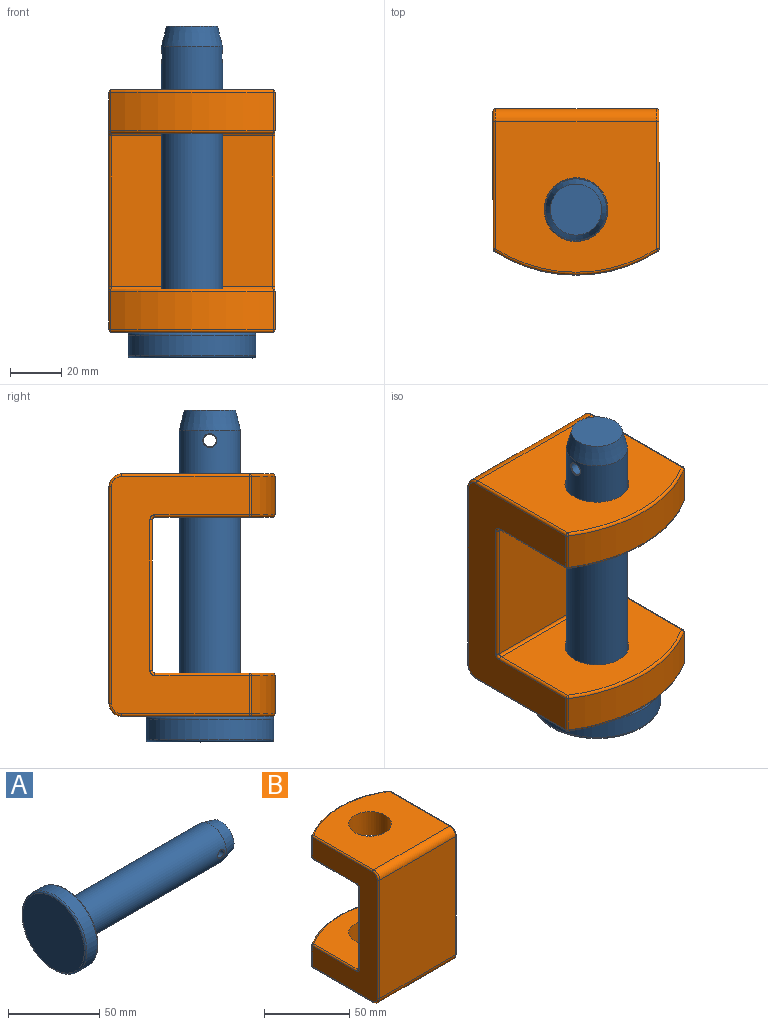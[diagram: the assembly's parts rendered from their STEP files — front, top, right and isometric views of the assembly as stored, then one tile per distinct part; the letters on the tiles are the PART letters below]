
ASSEMBLY  parts=2 mates=1
PART A: 12 faces, bbox 130x54.1x54.1 mm
  f0: cylinder r=12mm len=111mm, axis (1,0,0), area 8322.5mm2, adj f1,f8,f10,f11
  f1: torus R=13mm, axis (1,0,0), area 122mm2, adj f0,f2
  f2: plane 48x48mm, normal (1,0,0), area 1278.6mm2, adj f1,f3
  f3: torus R=24mm, axis (1,0,0), area 243.2mm2, adj f2,f4
  f4: cylinder r=25mm len=50mm, axis (1,0,0), area 1256.6mm2, adj f3,f5
  f5: torus R=24mm, axis (1,0,0), area 243.2mm2, adj f4,f6
  f6: plane 48x48mm, normal (-1,0,0), area 1809.6mm2, adj f5
  f7: plane 20x20mm, normal (1,0,0), area 314.2mm2, adj f8
  f8: cone r=10mm half-angle=14deg, axis (-1,0,0), area 569.9mm2, adj f0,f7
  f9: cylinder r=2.5mm len=23.6mm, axis (0,-1,0), area 365.8mm2, adj f10,f11
  f10: bspline ~5.5x5.4mm, area 5.5mm2, adj f0,f9
  f11: bspline ~5.5x5.4mm, area 5.5mm2, adj f0,f9
PART B: 53 faces, bbox 69.3x70.4x95.8 mm
  f0: plane 63x59mm, normal (0,0,1), area 3041.1mm2, adj f6,f12,f32,f42,f47
  f1: plane 63x59mm, normal (0,0,-1), area 2959.4mm2, adj f8,f33,f43,f48,f52
  f2: plane 63x46mm, normal (0,0,1), area 2222.1mm2, adj f9,f13,f21,f35,f36
  f3: plane 63x46mm, normal (0,0,-1), area 2222.1mm2, adj f11,f12,f19,f29,f30
  f4: plane 93x53.89mm, normal (1,0,0), area 2556.5mm2, adj f16,f17,f18,f19,f20,f21,f25,f26
  f5: plane 93x53.89mm, normal (-1,0,0), area 2556.5mm2, adj f22,f23,f28,f29,f36,f41,f44,f47
  f6: cylinder r=5mm len=63mm, axis (-1,0,0), area 494.8mm2, adj f0,f7,f25,f49
  f7: plane 85x63mm, normal (0,-1,0), area 5355mm2, adj f6,f8,f20,f51
  f8: cylinder r=5mm len=63mm, axis (-1,0,0), area 494.8mm2, adj f1,f7,f26,f50
  f9: cylinder r=1mm len=63mm, axis (-1,0,0), area 99mm2, adj f2,f10,f18,f28
  f10: plane 63x59mm, normal (0,1,0), area 3717mm2, adj f9,f11,f16,f22
  f11: cylinder r=1mm len=63mm, axis (-1,0,0), area 99mm2, adj f3,f10,f17,f23
  f12: cylinder r=12.5mm len=25mm, axis (0,0,1), area 1335.2mm2, adj f0,f3
  f13: cylinder r=12.5mm len=25mm, axis (0,0,1), area 1256.6mm2, adj f2,f52
  f14: cylinder r=60mm len=64.07mm, axis (0,0,1), area 1013.8mm2, adj f30,f31,f41,f42
  f15: cylinder r=60mm len=64.07mm, axis (0,0,1), area 1013.8mm2, adj f34,f35,f43,f44
  f16: cylinder r=1mm len=59mm, axis (0,0,-1), area 92.7mm2, adj f4,f10,f17,f18
  f17: torus R=2mm, axis (1,0,0), area 3.4mm2, adj f4,f11,f16,f19
  f18: torus R=2mm, axis (1,0,0), area 3.4mm2, adj f4,f9,f16,f21
  f19: cylinder r=1mm len=36.89mm, axis (0,-1,0), area 57.9mm2, adj f3,f4,f17,f24
  f20: cylinder r=1mm len=85mm, axis (0,0,1), area 133.5mm2, adj f4,f7,f25,f26
  f21: cylinder r=1mm len=36.89mm, axis (0,1,0), area 57.9mm2, adj f2,f4,f18,f27
  f22: cylinder r=1mm len=59mm, axis (0,0,1), area 92.7mm2, adj f5,f10,f23,f28
  f23: torus R=2mm, axis (1,0,0), area 3.4mm2, adj f5,f11,f22,f29
  f24: sphere r=1mm, area 1mm2, adj f19,f30,f31
  f25: torus R=4mm, axis (1,0,0), area 11.4mm2, adj f4,f6,f20,f32
  f26: torus R=4mm, axis (1,0,0), area 11.4mm2, adj f4,f8,f20,f33
  f27: sphere r=1mm, area 1mm2, adj f21,f34,f35
  f28: torus R=2mm, axis (1,0,0), area 3.4mm2, adj f5,f9,f22,f36
  f29: cylinder r=1mm len=36.89mm, axis (0,1,0), area 57.9mm2, adj f3,f5,f23,f37
  f30: torus R=59mm, axis (0,0,1), area 105.5mm2, adj f3,f14,f24,f37
  f31: cylinder r=1mm len=15mm, axis (0,0,1), area 15.1mm2, adj f4,f14,f24,f38
  f32: cylinder r=1mm len=49.89mm, axis (0,1,0), area 78.4mm2, adj f0,f4,f25,f38
  f33: cylinder r=1mm len=49.89mm, axis (0,-1,0), area 78.4mm2, adj f1,f4,f26,f39
  f34: cylinder r=1mm len=15mm, axis (0,0,1), area 15.1mm2, adj f4,f15,f27,f39
  f35: torus R=59mm, axis (0,0,1), area 105.5mm2, adj f2,f15,f27,f40
  f36: cylinder r=1mm len=36.89mm, axis (0,-1,0), area 57.9mm2, adj f2,f5,f28,f40
  f37: sphere r=1mm, area 1mm2, adj f29,f30,f41
  f38: sphere r=1mm, area 1mm2, adj f31,f32,f42
  f39: sphere r=1mm, area 1mm2, adj f33,f34,f43
  f40: sphere r=1mm, area 1mm2, adj f35,f36,f44
  f41: cylinder r=1mm len=15mm, axis (0,0,1), area 15.1mm2, adj f5,f14,f37,f45
  f42: torus R=59mm, axis (0,0,1), area 105.5mm2, adj f0,f14,f38,f45
  f43: torus R=59mm, axis (0,0,1), area 105.5mm2, adj f1,f15,f39,f46
  f44: cylinder r=1mm len=15mm, axis (0,0,1), area 15.1mm2, adj f5,f15,f40,f46
  f45: sphere r=1mm, area 1mm2, adj f41,f42,f47
  f46: sphere r=1mm, area 1mm2, adj f43,f44,f48
  f47: cylinder r=1mm len=49.89mm, axis (0,-1,0), area 78.4mm2, adj f0,f5,f45,f49
  f48: cylinder r=1mm len=49.89mm, axis (0,1,0), area 78.4mm2, adj f1,f5,f46,f50
  f49: torus R=4mm, axis (1,0,0), area 11.4mm2, adj f5,f6,f47,f51
  f50: torus R=4mm, axis (1,0,0), area 11.4mm2, adj f5,f8,f48,f51
  f51: cylinder r=1mm len=85mm, axis (0,0,-1), area 133.5mm2, adj f5,f7,f49,f50
  f52: torus R=13.5mm, axis (0,0,1), area 127mm2, adj f1,f13
PLACE A rot(axis=(-0.58,-0.58,-0.58),120deg) t=(167.95,-121.3,200.76)mm
PLACE B rot(axis=(0,0,-1),180deg) t=(200.45,-115.66,338.28)mm
MATE slider A.f8 <-> B.f12  axis (0,0,1) through (167.95,-72.01,439.75)mm
